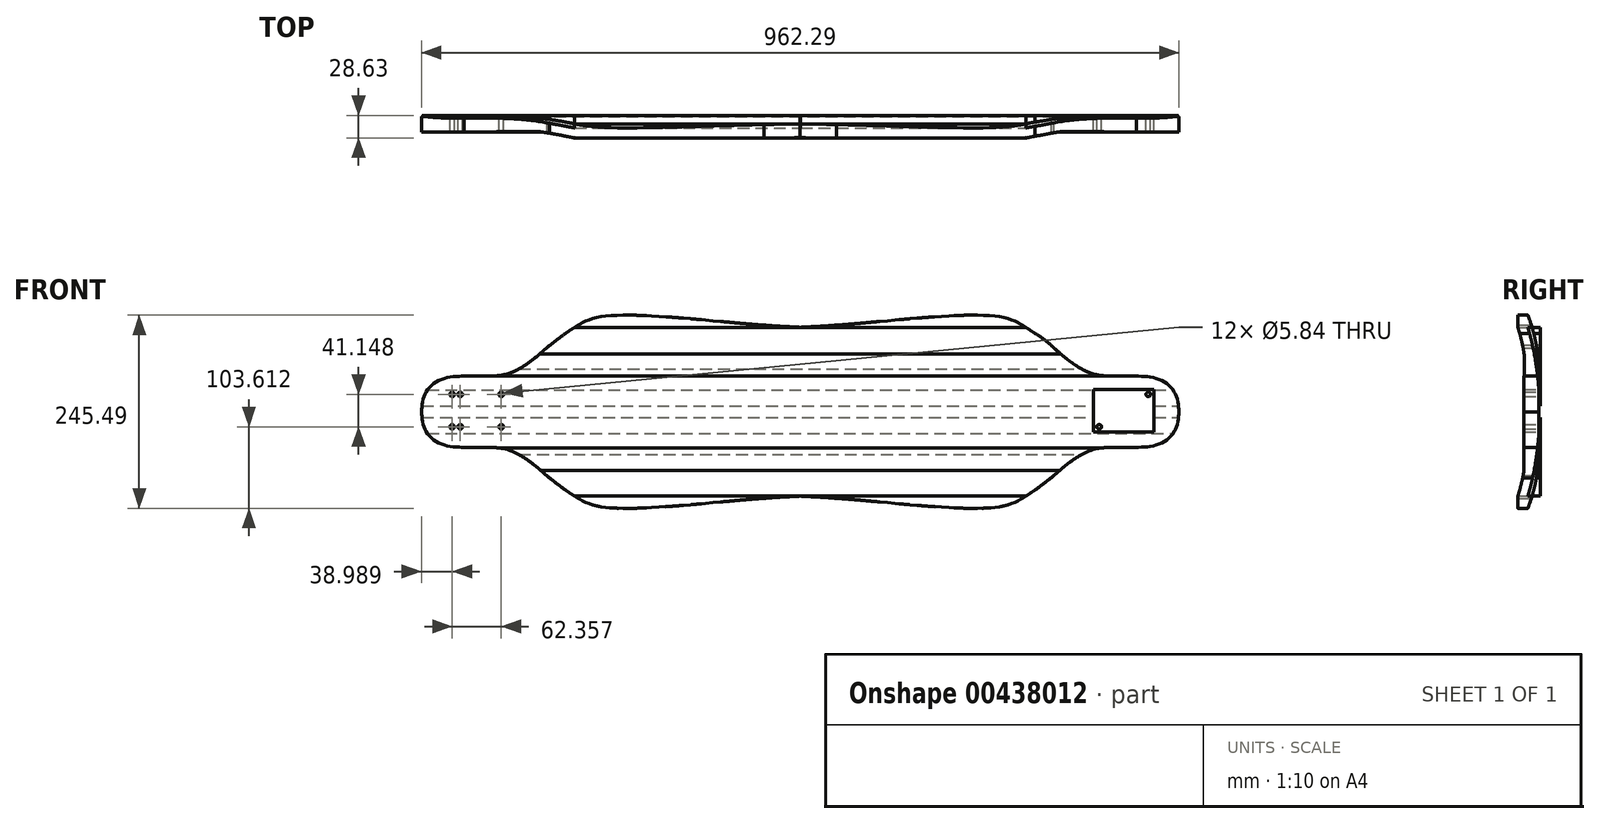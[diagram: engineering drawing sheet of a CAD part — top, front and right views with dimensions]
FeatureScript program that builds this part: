
annotation { "Feature Type Name" : "Feature", "Feature Type Description" : "" }
export const myFeature = defineFeature(function(context is Context, id is Id, definition is map)
    precondition{}
    {
        {
            var Q0;
            Q0=qCreatedBy(makeId("Front.planeOp"),FACE);
            var sketch = newSketch(context, id + "F0", { "sketchPlane" : qUnion([Q0])});
            skFitSpline(sketch, "E0.MirrorCS", {"points": [v(153.91, 111.97) * mm, v(126.22, 132.16) * mm, v(94.19, 138.32) * mm], "startDerivative": vector(-48.82, 48.29) * mm, "endDerivative": vector(-67.2, 5.62) * mm});
            skFitSpline(sketch, "E1.MirrorCS", {"points": [v(314.26, 80.32) * mm, v(259.22, 80.83) * mm, v(203.15, 79.33) * mm, v(126.22, 138.32) * mm], "startDerivative": vector(-184.89, 36.73) * mm, "endDerivative": vector(-208.9, 198.7) * mm});
            skFitSpline(sketch, "E2.MirrorCS", {"points": [v(153.91, -49.83) * mm, v(126.22, -70.02) * mm, v(94.19, -76.17) * mm], "startDerivative": vector(-48.82, -48.29) * mm, "endDerivative": vector(-67.2, -5.62) * mm});
            skFitSpline(sketch, "E3.MirrorCS", {"points": [v(314.26, -18.18) * mm, v(259.22, -18.69) * mm, v(203.15, -17.18) * mm, v(126.22, -76.17) * mm], "startDerivative": vector(-184.89, -36.73) * mm, "endDerivative": vector(-208.9, -198.7) * mm});
            skLineSegment(sketch, "E4", {"start": v(258.47, -14.52) * mm, "end": v(223.39, -14.47) * mm});
            skPoint(sketch, "E5.orphan", {"position": v(291.38, -20.7) * mm});
            skPoint(sketch, "E6.MirrorCS.0.internal.orphan", {"position": v(291.4, -22.2) * mm});
            skLineSegment(sketch, "E7.MirrorCS", {"start": v(258.47, 76.67) * mm, "end": v(223.39, 76.62) * mm});
            skPoint(sketch, "E8.orphan", {"position": v(288.53, 82.9) * mm});
            skPoint(sketch, "E9", {"position": v(-168.34, 36.66) * mm});
            skCircle(sketch, "E10.MirrorC", {"center": v(211.46, 11.94) * mm, "radius": 2.92 * mm});
            skCircle(sketch, "E11.MirrorC", {"center": v(273.82, 11.94) * mm, "radius": 2.92 * mm});
            skCircle(sketch, "E12.MirrorC", {"center": v(263.53, 11.94) * mm, "radius": 2.92 * mm});
            skCircle(sketch, "E13.MirrorC", {"center": v(273.82, 53.1) * mm, "radius": 2.92 * mm});
            skCircle(sketch, "E14.MirrorC", {"center": v(211.46, 53.1) * mm, "radius": 2.92 * mm});
            skCircle(sketch, "E15.MirrorC", {"center": v(263.53, 53.1) * mm, "radius": 2.92 * mm});
            skLineSegment(sketch, "E16.MirrorCS", {"start": v(281.05, 59.44) * mm, "end": v(204.1, 59.44) * mm});
            skLineSegment(sketch, "E17.MirrorCS", {"start": v(204.1, 59.44) * mm, "end": v(204.1, 5.6) * mm});
            skLineSegment(sketch, "E18.MirrorCS", {"start": v(281.05, 59.44) * mm, "end": v(281.05, 5.6) * mm});
            skLineSegment(sketch, "E19.MirrorCS", {"start": v(281.05, 5.6) * mm, "end": v(204.1, 5.6) * mm});
            skPoint(sketch, "E20.orphan", {"position": v(424.44, 75.27) * mm});
            skPoint(sketch, "E21.MirrorP", {"position": v(424.44, -13.13) * mm});
            skFitSpline(sketch, "E22.MirrorCS", {"points": [v(258.47, -14.52) * mm, v(279.76, -12.42) * mm, v(300.17, -2.22) * mm, v(310.38, 14.11) * mm, v(312.8, 31.07) * mm], "startDerivative": vector(67.24, 11.02) * mm, "endDerivative": vector(5.32, 67.13) * mm});
            skFitSpline(sketch, "E23.MirrorCS", {"points": [v(258.47, 76.67) * mm, v(279.76, 74.57) * mm, v(300.17, 64.36) * mm, v(310.38, 48.03) * mm, v(312.8, 31.07) * mm], "startDerivative": vector(67.24, -11.02) * mm, "endDerivative": vector(5.32, -67.13) * mm});
            skPoint(sketch, "E24.orphan", {"position": v(-761.13, 75.27) * mm});
            skPoint(sketch, "E25.orphan", {"position": v(315.71, 67.16) * mm});
            skPoint(sketch, "E26.end.orphan", {"position": v(315.71, -5.02) * mm});
            skPoint(sketch, "E27.orphan", {"position": v(-761.13, -13.13) * mm});
            skFitSpline(sketch, "E28.MirrorCS", {"points": [v(153.91, 111.97) * mm, v(118.25, 138.32) * mm, v(79.33, 152.54) * mm, v(-67.07, 145.75) * mm, v(-168.34, 138.32) * mm], "startDerivative": vector(-186.81, 155.51) * mm, "endDerivative": vector(-321.74, -14.8) * mm});
            skFitSpline(sketch, "E29.MirrorCS", {"points": [v(153.91, 111.97) * mm, v(118.25, 138.32) * mm, v(79.33, 152.54) * mm, v(-67.07, 145.75) * mm, v(-168.34, 138.32) * mm], "startDerivative": vector(-186.81, 155.51) * mm, "endDerivative": vector(-321.74, -14.8) * mm});
            skFitSpline(sketch, "E30.MirrorCS", {"points": [v(153.91, -49.83) * mm, v(118.25, -76.17) * mm, v(79.33, -90.4) * mm, v(-67.07, -83.6) * mm, v(-168.34, -76.17) * mm], "startDerivative": vector(-186.81, -155.51) * mm, "endDerivative": vector(-321.74, 14.8) * mm});
            skPoint(sketch, "E31.MirrorCS.end.orphan", {"position": v(-168.34, 127.37) * mm});
            skPoint(sketch, "E32.MirrorCS.end.orphan", {"position": v(-168.34, -65.22) * mm});
            skCircle(sketch, "E33.MirrorC", {"center": v(-610.5, 53.1) * mm, "radius": 2.92 * mm});
            skCircle(sketch, "E34.MirrorC", {"center": v(-600.21, 11.94) * mm, "radius": 2.92 * mm});
            skFitSpline(sketch, "E35.MirrorCS", {"points": [v(-490.6, -49.83) * mm, v(-462.9, -70.02) * mm, v(-430.87, -76.17) * mm], "startDerivative": vector(48.82, -48.29) * mm, "endDerivative": vector(67.2, -5.62) * mm});
            skFitSpline(sketch, "E36.MirrorCS", {"points": [v(-490.6, 111.97) * mm, v(-462.9, 132.16) * mm, v(-430.87, 138.32) * mm], "startDerivative": vector(48.82, 48.29) * mm, "endDerivative": vector(67.2, 5.62) * mm});
            skPoint(sketch, "E37.MirrorP", {"position": v(-652.4, 67.16) * mm});
            skPoint(sketch, "E38.MirrorP", {"position": v(-625.22, 82.9) * mm});
            skFitSpline(sketch, "E39.MirrorCS", {"points": [v(-490.6, 111.97) * mm, v(-454.93, 138.32) * mm, v(-416.02, 152.54) * mm, v(-269.61, 145.75) * mm, v(-168.34, 138.32) * mm], "startDerivative": vector(186.81, 155.51) * mm, "endDerivative": vector(321.74, -14.8) * mm});
            skCircle(sketch, "E40.MirrorC", {"center": v(-600.21, 53.1) * mm, "radius": 2.92 * mm});
            skCircle(sketch, "E41.MirrorC", {"center": v(-548.14, 53.1) * mm, "radius": 2.92 * mm});
            skCircle(sketch, "E42.MirrorC", {"center": v(-548.14, 11.94) * mm, "radius": 2.92 * mm});
            skCircle(sketch, "E43.MirrorC", {"center": v(-610.5, 11.94) * mm, "radius": 2.92 * mm});
            skPoint(sketch, "E44.MirrorP", {"position": v(-628.07, -20.7) * mm});
            skPoint(sketch, "E45.MirrorP", {"position": v(-652.4, -5.02) * mm});
            skFitSpline(sketch, "E46.MirrorCS", {"points": [v(-595.16, -14.52) * mm, v(-616.44, -12.42) * mm, v(-636.86, -2.22) * mm, v(-647.06, 14.11) * mm, v(-649.49, 31.07) * mm], "startDerivative": vector(-67.24, 11.02) * mm, "endDerivative": vector(-5.32, 67.13) * mm});
            skPoint(sketch, "E47.MirrorP", {"position": v(-628.09, -22.2) * mm});
            skFitSpline(sketch, "E48.MirrorCS", {"points": [v(-490.6, -49.83) * mm, v(-454.93, -76.17) * mm, v(-416.02, -90.4) * mm, v(-269.61, -83.6) * mm, v(-168.34, -76.17) * mm], "startDerivative": vector(186.81, -155.51) * mm, "endDerivative": vector(321.74, 14.8) * mm});
            skLineSegment(sketch, "E49.MirrorCS", {"start": v(-540.78, 59.44) * mm, "end": v(-540.78, 5.6) * mm});
            skFitSpline(sketch, "E50.MirrorCS", {"points": [v(-490.6, 111.97) * mm, v(-454.93, 138.32) * mm, v(-416.02, 152.54) * mm, v(-269.61, 145.75) * mm, v(-168.34, 138.32) * mm], "startDerivative": vector(186.81, 155.51) * mm, "endDerivative": vector(321.74, -14.8) * mm});
            skLineSegment(sketch, "E51.MirrorCS", {"start": v(-595.16, 76.67) * mm, "end": v(-560.08, 76.62) * mm});
            skLineSegment(sketch, "E52.MirrorCS", {"start": v(-595.16, -14.52) * mm, "end": v(-560.08, -14.47) * mm});
            skFitSpline(sketch, "E53.MirrorCS", {"points": [v(-650.94, -18.18) * mm, v(-595.9, -18.69) * mm, v(-539.83, -17.18) * mm, v(-462.9, -76.17) * mm], "startDerivative": vector(184.89, -36.73) * mm, "endDerivative": vector(208.9, -198.7) * mm});
            skLineSegment(sketch, "E54.MirrorCS", {"start": v(-617.74, 59.44) * mm, "end": v(-540.78, 59.44) * mm});
            skFitSpline(sketch, "E55.MirrorCS", {"points": [v(-650.94, 80.32) * mm, v(-595.9, 80.83) * mm, v(-539.83, 79.33) * mm, v(-462.9, 138.32) * mm], "startDerivative": vector(184.89, 36.73) * mm, "endDerivative": vector(208.9, 198.7) * mm});
            skLineSegment(sketch, "E56.MirrorCS", {"start": v(-617.74, 59.44) * mm, "end": v(-617.74, 5.6) * mm});
            skLineSegment(sketch, "E57.MirrorCS", {"start": v(-617.74, 5.6) * mm, "end": v(-540.78, 5.6) * mm});
            skFitSpline(sketch, "E58.MirrorCS", {"points": [v(-595.16, 76.67) * mm, v(-616.44, 74.57) * mm, v(-636.86, 64.36) * mm, v(-647.06, 48.03) * mm, v(-649.49, 31.07) * mm], "startDerivative": vector(-67.24, -11.02) * mm, "endDerivative": vector(-5.32, -67.13) * mm});
            skFitSpline(sketch, "E59", {"points": [v(-269.61, 145.75) * mm, v(-214.57, 141.12) * mm, v(-168.34, 139.72) * mm], "startDerivative": vector(107.74, -9.4) * mm, "endDerivative": vector(94.6, -2.55) * mm});
            skFitSpline(sketch, "E60.MirrorCS", {"points": [v(-67.07, 145.75) * mm, v(-122.12, 141.12) * mm, v(-168.34, 139.72) * mm], "startDerivative": vector(-107.74, -9.4) * mm, "endDerivative": vector(-94.6, -2.55) * mm});
            skFitSpline(sketch, "E61.MirrorCS", {"points": [v(-67.07, -83.6) * mm, v(-122.12, -78.98) * mm, v(-168.34, -77.58) * mm], "startDerivative": vector(-107.74, 9.4) * mm, "endDerivative": vector(-94.6, 2.55) * mm});
            skFitSpline(sketch, "E62.MirrorCS", {"points": [v(-269.61, -83.6) * mm, v(-214.57, -78.98) * mm, v(-168.34, -77.58) * mm], "startDerivative": vector(107.74, 9.4) * mm, "endDerivative": vector(94.6, 2.55) * mm});
            skPoint(sketch, "E63.orphan", {"position": v(-452.56, 31.07) * mm});
            skPoint(sketch, "E64.orphan", {"position": v(115.87, 31.07) * mm});
            skLineSegment(sketch, "E65.trimOffspring", {"start": v(-168.34, -76.17) * mm, "end": v(-168.34, -77.64) * mm});
            skPoint(sketch, "E66.start.orphan", {"position": v(-168.34, 150.96) * mm});
            skSolve(sketch);
        }
        {
            var Q0;
            Q0=makeQuery(id+"F0.imprint","IMPRINT",FACE,{"disambiguationData":[TD([[makeQuery(id+"F0.imprint","IMPRINT",EDGE,{"derivedFrom":sQuery(id+"F0.wireOp",EDGE,"54694fe5-f969-434b-b929-3ccada8eebf9")}),-1.0]])]});
            var Q1;
            Q1=makeQuery(id+"F0.imprint","IMPRINT",FACE,{"disambiguationData":[TD([[makeQuery(id+"F0.imprint","IMPRINT",EDGE,{"derivedFrom":sQuery(id+"F0.wireOp",EDGE,"02af59b5-e7f6-4803-9d26-3b46dd477805.right")}),-1.0]])]});
            var Q2;
            {var subQ0=sQuery(id+"F0.wireOp",EDGE,"062809b9-a678-4541-9586-a59974c6fc33.bottom");Q2=makeQuery(id+"F0.imprint","IMPRINT",FACE,{"disambiguationData":[TD([[makeQuery(id+"F0.imprint","IMPRINT",EDGE,{"derivedFrom":subQ0}),-1.0]])]});}
            var Q3;
            Q3=makeQuery(id+"F0.imprint","IMPRINT",FACE,{"disambiguationData":[TD([[makeQuery(id+"F0.imprint","IMPRINT",EDGE,{"derivedFrom":sQuery(id+"F0.wireOp",EDGE,"92bb7d47-26f2-429a-bf82-6a459e636457")}),-1.0]])]});
            var Q4;
            Q4=makeQuery(id+"F0.imprint","IMPRINT",FACE,{"disambiguationData":[TD([[makeQuery(id+"F0.imprint","IMPRINT",EDGE,{"derivedFrom":sQuery(id+"F0.wireOp",EDGE,"E10.MirrorC")}),1.0]])]});
            var Q5;
            Q5=makeQuery(id+"F0.imprint","IMPRINT",FACE,{"disambiguationData":[TD([[makeQuery(id+"F0.imprint","IMPRINT",EDGE,{"derivedFrom":sQuery(id+"F0.wireOp",EDGE,"89cd0182-1944-4f00-9323-803960b5a9c0")}),-1.0]])]});
            var Q6;
            Q6=makeQuery(id+"F0.imprint","IMPRINT",FACE,{"disambiguationData":[TD([[makeQuery(id+"F0.imprint","IMPRINT",EDGE,{"derivedFrom":sQuery(id+"F0.wireOp",EDGE,"062809b9-a678-4541-9586-a59974c6fc33.left")}),1.0]])]});
            var Q7;
            {var subQ0=sQuery(id+"F0.wireOp",EDGE,"b9591a49-4a40-4ac3-9c40-6eddea82a4450.MirrorCS");Q7=makeQuery(id+"F0.imprint","IMPRINT",FACE,{"disambiguationData":[TD([[makeQuery(id+"F0.imprint","IMPRINT",EDGE,{"derivedFrom":subQ0}),-1.0]])]});}
            var Q8;
            {var subQ0=sQuery(id+"F0.wireOp",EDGE,"f067fed3-db68-4427-a3f0-daf9bd1214f3");Q8=makeQuery(id+"F0.imprint","IMPRINT",FACE,{"disambiguationData":[TD([[makeQuery(id+"F0.imprint","IMPRINT",EDGE,{"derivedFrom":subQ0}),1.0]])]});}
            var Q9;
            {var subQ0=sQuery(id+"F0.wireOp",EDGE,"E32.MirrorCS");Q9=makeQuery(id+"F0.imprint","IMPRINT",FACE,{"disambiguationData":[TD([[makeQuery(id+"F0.imprint","IMPRINT",EDGE,{"derivedFrom":subQ0}),-1.0]])]});}
            var Q10;
            {var subQ0=sQuery(id+"F0.wireOp",EDGE,"E31.MirrorCS");Q10=makeQuery(id+"F0.imprint","IMPRINT",FACE,{"disambiguationData":[TD([[makeQuery(id+"F0.imprint","IMPRINT",EDGE,{"derivedFrom":subQ0}),1.0]])]});}
            var Q11;
            {var subQ12=sQuery(id+"F0.wireOp",EDGE,"E1.MirrorCS");Q11=makeQuery(id+"F0.imprint","IMPRINT",FACE,{"disambiguationData":[TD([[makeQuery(id+"F0.imprint","IMPRINT",EDGE,{"derivedFrom":subQ12}),1.0]])]});}
            var Q12;
            Q12=makeQuery(id+"F0.imprint","IMPRINT",FACE,{"disambiguationData":[TD([[makeQuery(id+"F0.imprint","IMPRINT",EDGE,{"derivedFrom":sQuery(id+"F0.wireOp",EDGE,"E46.MirrorCS")}),-1.0]])]});
            var Q13;
            {var subQ0=sQuery(id+"F0.wireOp",EDGE,"E359.MirrorCS");Q13=makeQuery(id+"F0.imprint","IMPRINT",FACE,{"disambiguationData":[TD([[makeQuery(id+"F0.imprint","IMPRINT",EDGE,{"derivedFrom":subQ0}),1.0]])]});}
            var Q14;
            {var subQ0=sQuery(id+"F0.wireOp",EDGE,"E358.MirrorCS");Q14=makeQuery(id+"F0.imprint","IMPRINT",FACE,{"disambiguationData":[TD([[makeQuery(id+"F0.imprint","IMPRINT",EDGE,{"derivedFrom":subQ0}),-1.0]])]});}
            var Q15;
            Q15=makeQuery(id+"F0.imprint","IMPRINT",FACE,{"disambiguationData":[TD([[makeQuery(id+"F0.imprint","IMPRINT",EDGE,{"derivedFrom":sQuery(id+"F0.wireOp",EDGE,"E13.MirrorC")}),1.0]])]});
            var Q16;
            Q16=makeQuery(id+"F0.imprint","IMPRINT",FACE,{"disambiguationData":[TD([[makeQuery(id+"F0.imprint","IMPRINT",EDGE,{"derivedFrom":sQuery(id+"F0.wireOp",EDGE,"E34.MirrorC")}),-1.0]])]});
            var Q17;
            Q17=makeQuery(id+"F0.imprint","IMPRINT",FACE,{"disambiguationData":[TD([[makeQuery(id+"F0.imprint","IMPRINT",EDGE,{"derivedFrom":sQuery(id+"F0.wireOp",EDGE,"E33.MirrorC")}),-1.0]])]});
            extrude(context, id + "F1", {"entities" : qUnion([Q0, Q1, Q2, Q3, Q4, Q5, Q6, Q7, Q8, Q9, Q10, Q11, Q12, Q13, Q14, Q15, Q16, Q17]), "depth" : 50.8 * mm});
        }
        {
            var Q0;
            Q0=makeQuery(id+"F1.opExtrude","CAP_FACE",FACE,{"disambiguationData":[OSD([sQuery(id+"F0.wireOp",EDGE,"02af59b5-e7f6-4803-9d26-3b46dd477805.left"),sQuery(id+"F0.wireOp",EDGE,"02af59b5-e7f6-4803-9d26-3b46dd477805.right"),sQuery(id+"F0.wireOp",EDGE,"54694fe5-f969-434b-b929-3ccada8eebf9"),sQuery(id+"F0.wireOp",EDGE,"9572b309-95b0-4d00-b009-9f7e73c3226a"),sQuery(id+"F0.wireOp",EDGE,"9ed70d03-f706-47da-8b4f-a9a363b289d10.MirrorCS"),sQuery(id+"F0.wireOp",EDGE,"E0.MirrorCS"),sQuery(id+"F0.wireOp",EDGE,"E1.MirrorCS"),sQuery(id+"F0.wireOp",EDGE,"E2.MirrorCS"),sQuery(id+"F0.wireOp",EDGE,"E3.MirrorCS"),sQuery(id+"F0.wireOp",EDGE,"E4"),sQuery(id+"F0.wireOp",EDGE,"E26"),sQuery(id+"F0.wireOp",EDGE,"E7.MirrorCS"),sQuery(id+"F0.wireOp",EDGE,"cba3995b-21b8-48ba-a17e-b84a468ee1200.MirrorCS"),sQuery(id+"F0.wireOp",EDGE,"9455ca8d-976e-4d45-868c-3e5ceae797750.MirrorCS"),sQuery(id+"F0.wireOp",EDGE,"bb437472-1cce-4c1d-80da-beb2af860ac20.MirrorCS"),sQuery(id+"F0.wireOp",EDGE,"1ed70d3d-ef56-45d5-8113-0e0346001ab10.MirrorCS"),sQuery(id+"F0.wireOp",EDGE,"96e13706-5ee7-4921-8a0b-7c01300654cf0.MirrorCS"),sQuery(id+"F0.wireOp",EDGE,"5faff583-b4fc-4a09-a63c-e9ec7a417d71.trimOffspring"),sQuery(id+"F0.wireOp",EDGE,"f067fed3-db68-4427-a3f0-daf9bd1214f3"),sQuery(id+"F0.wireOp",EDGE,"b9591a49-4a40-4ac3-9c40-6eddea82a4450.MirrorCS"),sQuery(id+"F0.wireOp",EDGE,"E32.MirrorCS"),sQuery(id+"F0.wireOp",EDGE,"E31.MirrorCS")])],"isStart":false});
            var sketch = newSketch(context, id + "F2", { "sketchPlane" : qUnion([Q0])});
            skLineSegment(sketch, "E67.bottom", {"start": v(-617.74, 56.54) * mm, "end": v(-540.78, 56.54) * mm});
            skLineSegment(sketch, "E67.top", {"start": v(-617.74, 2.69) * mm, "end": v(-540.78, 2.69) * mm});
            skLineSegment(sketch, "E67.left", {"start": v(-617.74, 56.54) * mm, "end": v(-617.74, 2.69) * mm});
            skLineSegment(sketch, "E67.right", {"start": v(-540.78, 56.54) * mm, "end": v(-540.78, 2.69) * mm});
            skCircle(sketch, "E68", {"center": v(-610.37, 50.19) * mm, "radius": 2.92 * mm});
            skCircle(sketch, "E69", {"center": v(-610.37, 9.04) * mm, "radius": 2.92 * mm});
            skCircle(sketch, "E70", {"center": v(-600.21, 50.19) * mm, "radius": 2.92 * mm});
            skCircle(sketch, "E71", {"center": v(-600.21, 9.04) * mm, "radius": 2.92 * mm});
            skCircle(sketch, "E72", {"center": v(-548.14, 9.04) * mm, "radius": 2.92 * mm});
            skCircle(sketch, "E73", {"center": v(-548.14, 50.19) * mm, "radius": 2.92 * mm});
            skLineSegment(sketch, "E74", {"start": v(-166.89, 125.92) * mm, "end": v(-166.89, -66.71) * mm});
            skLineSegment(sketch, "E75.MirrorCS", {"start": v(283.96, 56.54) * mm, "end": v(207, 56.54) * mm});
            skLineSegment(sketch, "E76.MirrorCS", {"start": v(207, 56.54) * mm, "end": v(207, 2.69) * mm});
            skLineSegment(sketch, "E77.MirrorCS", {"start": v(283.96, 2.69) * mm, "end": v(207, 2.69) * mm});
            skLineSegment(sketch, "E78.MirrorCS", {"start": v(283.96, 56.54) * mm, "end": v(283.96, 2.69) * mm});
            skCircle(sketch, "E79.MirrorC", {"center": v(276.6, 50.19) * mm, "radius": 2.92 * mm});
            skCircle(sketch, "E80.MirrorC", {"center": v(276.6, 9.04) * mm, "radius": 2.92 * mm});
            skCircle(sketch, "E81.MirrorC", {"center": v(266.43, 50.19) * mm, "radius": 2.92 * mm});
            skCircle(sketch, "E82.MirrorC", {"center": v(266.43, 9.04) * mm, "radius": 2.92 * mm});
            skCircle(sketch, "E83.MirrorC", {"center": v(214.36, 9.04) * mm, "radius": 2.92 * mm});
            skCircle(sketch, "E84.MirrorC", {"center": v(214.36, 50.19) * mm, "radius": 2.92 * mm});
            skSolve(sketch);
        }
        {
            var Q0;
            Q0=makeQuery(id+"F2.imprint","IMPRINT",FACE,{"disambiguationData":[TD([[makeQuery(id+"F2.imprint","IMPRINT",EDGE,{"derivedFrom":sQuery(id+"F2.wireOp",EDGE,"E68")}),1.0]])]});
            var Q1;
            Q1=makeQuery(id+"F2.imprint","IMPRINT",FACE,{"disambiguationData":[TD([[makeQuery(id+"F2.imprint","IMPRINT",EDGE,{"derivedFrom":sQuery(id+"F2.wireOp",EDGE,"E70")}),1.0]])]});
            var Q2;
            Q2=makeQuery(id+"F2.imprint","IMPRINT",FACE,{"disambiguationData":[TD([[makeQuery(id+"F2.imprint","IMPRINT",EDGE,{"derivedFrom":sQuery(id+"F2.wireOp",EDGE,"E71")}),1.0]])]});
            var Q3;
            Q3=makeQuery(id+"F2.imprint","IMPRINT",FACE,{"disambiguationData":[TD([[makeQuery(id+"F2.imprint","IMPRINT",EDGE,{"derivedFrom":sQuery(id+"F2.wireOp",EDGE,"E69")}),1.0]])]});
            var Q4;
            Q4=makeQuery(id+"F2.imprint","IMPRINT",FACE,{"disambiguationData":[TD([[makeQuery(id+"F2.imprint","IMPRINT",EDGE,{"derivedFrom":sQuery(id+"F2.wireOp",EDGE,"E72")}),1.0]])]});
            var Q5;
            Q5=makeQuery(id+"F2.imprint","IMPRINT",FACE,{"disambiguationData":[TD([[makeQuery(id+"F2.imprint","IMPRINT",EDGE,{"derivedFrom":sQuery(id+"F2.wireOp",EDGE,"E73")}),1.0]])]});
            var Q6;
            Q6=makeQuery(id+"F2.imprint","IMPRINT",FACE,{"disambiguationData":[TD([[makeQuery(id+"F2.imprint","IMPRINT",EDGE,{"derivedFrom":sQuery(id+"F2.wireOp",EDGE,"E84.MirrorC")}),-1.0]])]});
            var Q7;
            Q7=makeQuery(id+"F2.imprint","IMPRINT",FACE,{"disambiguationData":[TD([[makeQuery(id+"F2.imprint","IMPRINT",EDGE,{"derivedFrom":sQuery(id+"F2.wireOp",EDGE,"E83.MirrorC")}),-1.0]])]});
            var Q8;
            Q8=makeQuery(id+"F2.imprint","IMPRINT",FACE,{"disambiguationData":[TD([[makeQuery(id+"F2.imprint","IMPRINT",EDGE,{"derivedFrom":sQuery(id+"F2.wireOp",EDGE,"E82.MirrorC")}),-1.0]])]});
            var Q9;
            Q9=makeQuery(id+"F2.imprint","IMPRINT",FACE,{"disambiguationData":[TD([[makeQuery(id+"F2.imprint","IMPRINT",EDGE,{"derivedFrom":sQuery(id+"F2.wireOp",EDGE,"E80.MirrorC")}),-1.0]])]});
            var Q10;
            Q10=makeQuery(id+"F2.imprint","IMPRINT",FACE,{"disambiguationData":[TD([[makeQuery(id+"F2.imprint","IMPRINT",EDGE,{"derivedFrom":sQuery(id+"F2.wireOp",EDGE,"E79.MirrorC")}),-1.0]])]});
            var Q11;
            Q11=makeQuery(id+"F2.imprint","IMPRINT",FACE,{"disambiguationData":[TD([[makeQuery(id+"F2.imprint","IMPRINT",EDGE,{"derivedFrom":sQuery(id+"F2.wireOp",EDGE,"E81.MirrorC")}),-1.0]])]});
            extrude(context, id + "F3", {"entities" : qUnion([Q0, Q1, Q2, Q3, Q4, Q5, Q6, Q7, Q8, Q9, Q10, Q11]), "operationType" : NewBodyOperationType.REMOVE, "oppositeDirection" : true, "depth" : 25.4 * mm});
        }
        {
            var Q0;
            Q0=makeQuery(id+"F1.opExtrude","CAP_FACE",FACE,{"disambiguationData":[OSD([sQuery(id+"F0.wireOp",EDGE,"54694fe5-f969-434b-b929-3ccada8eebf9"),sQuery(id+"F0.wireOp",EDGE,"9572b309-95b0-4d00-b009-9f7e73c3226a"),sQuery(id+"F0.wireOp",EDGE,"9ed70d03-f706-47da-8b4f-a9a363b289d10.MirrorCS"),sQuery(id+"F0.wireOp",EDGE,"E0.MirrorCS"),sQuery(id+"F0.wireOp",EDGE,"E1.MirrorCS"),sQuery(id+"F0.wireOp",EDGE,"E2.MirrorCS"),sQuery(id+"F0.wireOp",EDGE,"E3.MirrorCS"),sQuery(id+"F0.wireOp",EDGE,"E4"),sQuery(id+"F0.wireOp",EDGE,"E7.MirrorCS"),sQuery(id+"F0.wireOp",EDGE,"9455ca8d-976e-4d45-868c-3e5ceae797750.MirrorCS"),sQuery(id+"F0.wireOp",EDGE,"5faff583-b4fc-4a09-a63c-e9ec7a417d71.trimOffspring"),sQuery(id+"F0.wireOp",EDGE,"f067fed3-db68-4427-a3f0-daf9bd1214f3"),sQuery(id+"F0.wireOp",EDGE,"b9591a49-4a40-4ac3-9c40-6eddea82a4450.MirrorCS"),sQuery(id+"F0.wireOp",EDGE,"E32.MirrorCS"),sQuery(id+"F0.wireOp",EDGE,"E31.MirrorCS"),sQuery(id+"F0.wireOp",EDGE,"92bb7d47-26f2-429a-bf82-6a459e636457"),sQuery(id+"F0.wireOp",EDGE,"b6ba227c-8afe-4edb-aedd-f0549fda6e15"),sQuery(id+"F0.wireOp",EDGE,"793bed87-008b-41f4-bf6e-c205d1063800"),sQuery(id+"F0.wireOp",EDGE,"28036a85-de49-4989-b8b5-f112d6133179"),sQuery(id+"F0.wireOp",EDGE,"89cd0182-1944-4f00-9323-803960b5a9c0"),sQuery(id+"F0.wireOp",EDGE,"6373697f-7fe0-442c-b118-95b429602822"),sQuery(id+"F0.wireOp",EDGE,"E10.MirrorC"),sQuery(id+"F0.wireOp",EDGE,"E11.MirrorC"),sQuery(id+"F0.wireOp",EDGE,"E12.MirrorC"),sQuery(id+"F0.wireOp",EDGE,"E13.MirrorC"),sQuery(id+"F0.wireOp",EDGE,"E14.MirrorC"),sQuery(id+"F0.wireOp",EDGE,"E15.MirrorC"),sQuery(id+"F0.wireOp",EDGE,"cea14af6-60e8-406b-8ace-559b2c7d7bdf"),sQuery(id+"F0.wireOp",EDGE,"2c7a5f25-ea35-4496-83f1-23e8682bbf5f1.MirrorCS"),sQuery(id+"F0.wireOp",EDGE,"2c7a5f25-ea35-4496-83f1-23e8682bbf5f5.MirrorC"),sQuery(id+"F0.wireOp",EDGE,"2c7a5f25-ea35-4496-83f1-23e8682bbf5f8.MirrorCS"),sQuery(id+"F0.wireOp",EDGE,"E22.MirrorCS"),sQuery(id+"F0.wireOp",EDGE,"E23.MirrorCS")])],"isStart":false});
            extrude(context, id + "F4", {"entities" : qUnion([Q0]), "depth" : 1.27 * mm});
        }
        {
            var Q0;
            Q0=makeQuery(id+"F4.opExtrude","SWEPT_BODY",BODY,{"disambiguationData":[OSD([sQuery(id+"F0.wireOp",EDGE,"54694fe5-f969-434b-b929-3ccada8eebf9"),sQuery(id+"F0.wireOp",EDGE,"9572b309-95b0-4d00-b009-9f7e73c3226a"),sQuery(id+"F0.wireOp",EDGE,"9ed70d03-f706-47da-8b4f-a9a363b289d10.MirrorCS"),sQuery(id+"F0.wireOp",EDGE,"E0.MirrorCS"),sQuery(id+"F0.wireOp",EDGE,"E1.MirrorCS"),sQuery(id+"F0.wireOp",EDGE,"E2.MirrorCS"),sQuery(id+"F0.wireOp",EDGE,"E3.MirrorCS"),sQuery(id+"F0.wireOp",EDGE,"E4"),sQuery(id+"F0.wireOp",EDGE,"E7.MirrorCS"),sQuery(id+"F0.wireOp",EDGE,"9455ca8d-976e-4d45-868c-3e5ceae797750.MirrorCS"),sQuery(id+"F0.wireOp",EDGE,"5faff583-b4fc-4a09-a63c-e9ec7a417d71.trimOffspring"),sQuery(id+"F0.wireOp",EDGE,"f067fed3-db68-4427-a3f0-daf9bd1214f3"),sQuery(id+"F0.wireOp",EDGE,"b9591a49-4a40-4ac3-9c40-6eddea82a4450.MirrorCS"),sQuery(id+"F0.wireOp",EDGE,"E32.MirrorCS"),sQuery(id+"F0.wireOp",EDGE,"E31.MirrorCS"),sQuery(id+"F0.wireOp",EDGE,"92bb7d47-26f2-429a-bf82-6a459e636457"),sQuery(id+"F0.wireOp",EDGE,"b6ba227c-8afe-4edb-aedd-f0549fda6e15"),sQuery(id+"F0.wireOp",EDGE,"793bed87-008b-41f4-bf6e-c205d1063800"),sQuery(id+"F0.wireOp",EDGE,"28036a85-de49-4989-b8b5-f112d6133179"),sQuery(id+"F0.wireOp",EDGE,"89cd0182-1944-4f00-9323-803960b5a9c0"),sQuery(id+"F0.wireOp",EDGE,"6373697f-7fe0-442c-b118-95b429602822"),sQuery(id+"F0.wireOp",EDGE,"E10.MirrorC"),sQuery(id+"F0.wireOp",EDGE,"E11.MirrorC"),sQuery(id+"F0.wireOp",EDGE,"E12.MirrorC"),sQuery(id+"F0.wireOp",EDGE,"E13.MirrorC"),sQuery(id+"F0.wireOp",EDGE,"E14.MirrorC"),sQuery(id+"F0.wireOp",EDGE,"E15.MirrorC"),sQuery(id+"F0.wireOp",EDGE,"cea14af6-60e8-406b-8ace-559b2c7d7bdf"),sQuery(id+"F0.wireOp",EDGE,"2c7a5f25-ea35-4496-83f1-23e8682bbf5f1.MirrorCS"),sQuery(id+"F0.wireOp",EDGE,"2c7a5f25-ea35-4496-83f1-23e8682bbf5f5.MirrorC"),sQuery(id+"F0.wireOp",EDGE,"2c7a5f25-ea35-4496-83f1-23e8682bbf5f8.MirrorCS"),sQuery(id+"F0.wireOp",EDGE,"E22.MirrorCS"),sQuery(id+"F0.wireOp",EDGE,"E23.MirrorCS")])]});
            deleteBodies(context, id + "F5", {"entities" : qUnion([Q0])});
        }
        {
            var Q0;
            Q0=qCreatedBy(makeId("Right.planeOp"),FACE);
            cPlane(context, id + "F6", {"entities" : qUnion([Q0]), "cplaneType" : CPlaneType.OFFSET, "offset" : 330.2 * mm, "width" : 152.4 * mm, "height" : 152.4 * mm});
        }
        {
            var Q0;
            Q0=qCreatedBy(id+"F6.planeOp",FACE);
            var sketch = newSketch(context, id + "F7", { "sketchPlane" : qUnion([Q0])});
            skLineSegment(sketch, "E85.bottom", {"start": v(-48.15, -76.19) * mm, "end": v(0, -76.19) * mm});
            skLineSegment(sketch, "E85.right", {"start": v(0, -76.19) * mm, "end": v(0, 123.87) * mm});
            skFitSpline(sketch, "E86.MirrorCS", {"points": [v(-15.93, 138.33) * mm, v(-6.62, 98.44) * mm, v(0, 38.3) * mm], "startDerivative": vector(23.4, -79.2) * mm, "endDerivative": vector(9.06, -120.52) * mm});
            skLineSegment(sketch, "E87", {"start": v(-15.93, -76.19) * mm, "end": v(-28.63, -76.19) * mm});
            skFitSpline(sketch, "E88", {"points": [v(-28.63, -76.19) * mm, v(-20.04, -37.9) * mm, v(-17.25, 31.07) * mm], "startDerivative": vector(27.5, 88.82) * mm, "endDerivative": vector(-0.53, 124.55) * mm});
            skFitSpline(sketch, "E89.MirrorCS", {"points": [v(-28.63, 138.33) * mm, v(-20.04, 100.04) * mm, v(-17.25, 31.07) * mm], "startDerivative": vector(27.5, -88.82) * mm, "endDerivative": vector(-0.53, -124.55) * mm});
            skLineSegment(sketch, "E90", {"start": v(-28.63, 138.33) * mm, "end": v(-28.34, 138.33) * mm});
            skLineSegment(sketch, "E91", {"start": v(0, 23.84) * mm, "end": v(0, 38.3) * mm});
            skLineSegment(sketch, "E92", {"start": v(-17.15, 54.74) * mm, "end": v(-17.15, 7.4) * mm});
            skLineSegment(sketch, "E93", {"start": v(0, 123.87) * mm, "end": v(0, 138.52) * mm});
            skLineSegment(sketch, "E94", {"start": v(-15.93, 138.33) * mm, "end": v(0, 138.33) * mm});
            skLineSegment(sketch, "E95", {"start": v(0, 138.33) * mm, "end": v(-15.93, 138.33) * mm});
            skLineSegment(sketch, "E96", {"start": v(-52.48, 138.33) * mm, "end": v(-53.99, -76.19) * mm});
            skLineSegment(sketch, "E97", {"start": v(-53.99, -76.19) * mm, "end": v(-48.15, -76.19) * mm});
            skLineSegment(sketch, "E98", {"start": v(-22.28, 138.33) * mm, "end": v(-22.28, 155.69) * mm});
            skLineSegment(sketch, "E99", {"start": v(-28.63, 142.12) * mm, "end": v(-28.63, 154.1) * mm});
            skLineSegment(sketch, "E100", {"start": v(-28.63, 154.1) * mm, "end": v(-15.93, 154.1) * mm});
            skArc(sketch, "E101.filletArc", {"start": v(-28.63, 142.12) * mm, "mid": v(-28.36, 138.43) * mm, "end": v(-27.55, 134.81) * mm});
            skLineSegment(sketch, "E102.MirrorCS", {"start": v(-28.63, -76.19) * mm, "end": v(-28.34, -76.19) * mm});
            skArc(sketch, "E103.MirrorCS", {"start": v(-28.63, -79.98) * mm, "mid": v(-28.36, -76.29) * mm, "end": v(-27.55, -72.67) * mm});
            skLineSegment(sketch, "E104.MirrorCS", {"start": v(-15.93, -76.19) * mm, "end": v(0, -76.19) * mm});
            skFitSpline(sketch, "E105.MirrorCS", {"points": [v(-28.63, -76.19) * mm, v(-20.04, -37.9) * mm, v(-17.25, 31.07) * mm], "startDerivative": vector(27.5, 88.82) * mm, "endDerivative": vector(-0.53, 124.55) * mm});
            skLineSegment(sketch, "E106.MirrorCS", {"start": v(-28.63, -91.95) * mm, "end": v(-15.93, -91.95) * mm});
            skFitSpline(sketch, "E107.MirrorCS", {"points": [v(-15.93, -76.19) * mm, v(-6.62, -36.3) * mm, v(0, 23.84) * mm], "startDerivative": vector(23.4, 79.2) * mm, "endDerivative": vector(9.06, 120.52) * mm});
            skLineSegment(sketch, "E108.MirrorCS", {"start": v(0, -76.19) * mm, "end": v(-52.48, -76.19) * mm});
            skLineSegment(sketch, "E109.MirrorCS", {"start": v(0, -61.73) * mm, "end": v(0, -76.37) * mm});
            skLineSegment(sketch, "E110.MirrorCS", {"start": v(-28.63, -79.98) * mm, "end": v(-28.63, -91.95) * mm});
            skLineSegment(sketch, "E111.MirrorCS", {"start": v(-22.28, -76.19) * mm, "end": v(-22.28, -93.54) * mm});
            skLineSegment(sketch, "E112", {"start": v(-52.48, 138.33) * mm, "end": v(-52.48, 162.03) * mm});
            skLineSegment(sketch, "E113", {"start": v(-52.48, 162.03) * mm, "end": v(24.08, 159.46) * mm});
            skLineSegment(sketch, "E114", {"start": v(24.08, 159.46) * mm, "end": v(-0.26, 137.33) * mm});
            skLineSegment(sketch, "E115", {"start": v(-53.99, -76.19) * mm, "end": v(-80.3, -110.8) * mm});
            skLineSegment(sketch, "E116", {"start": v(-80.3, -110.8) * mm, "end": v(20.37, -120.62) * mm});
            skLineSegment(sketch, "E117", {"start": v(20.37, -120.62) * mm, "end": v(0, -76.19) * mm});
            skLineSegment(sketch, "E118", {"start": v(-1.66, 3.73) * mm, "end": v(-1.66, 31.07) * mm});
            skPoint(sketch, "E118.endSnap0", {"position": v(0, 31.07) * mm});
            skLineSegment(sketch, "E119", {"start": v(-1.66, 31.07) * mm, "end": v(-1.91, 31.11) * mm});
            skLineSegment(sketch, "E120.MirrorCS", {"start": v(-1.66, 58.41) * mm, "end": v(-1.66, 31.07) * mm});
            skLineSegment(sketch, "E121", {"start": v(-18.61, 31.07) * mm, "end": v(-19.22, 31.07) * mm});
            skPoint(sketch, "E122.MirrorCS.end.orphan", {"position": v(-18.61, 31.07) * mm});
            skPoint(sketch, "E122.MirrorCS.start.orphan", {"position": v(-18.61, 84.71) * mm});
            skPoint(sketch, "E123.start.orphan", {"position": v(-18.61, -22.57) * mm});
            skLineSegment(sketch, "E124", {"start": v(-20.8, -43.48) * mm, "end": v(-20.6, 104.17) * mm});
            skLineSegment(sketch, "E125", {"start": v(-20.6, 104.17) * mm, "end": v(-21.65, 104) * mm});
            skPoint(sketch, "E126.MirrorCS.end.orphan", {"position": v(-19.5, 31.07) * mm});
            skPoint(sketch, "E126.MirrorCS.start.orphan", {"position": v(-19.5, 95.16) * mm});
            skPoint(sketch, "E127.start.orphan", {"position": v(-19.5, -33.02) * mm});
            skLineSegment(sketch, "E128", {"start": v(-1.66, 3.73) * mm, "end": v(-1.66, -23.27) * mm});
            skFitSpline(sketch, "E129", {"points": [v(-1.66, -23.27) * mm, v(-6.5, -60.55) * mm, v(-15.93, -91.95) * mm], "startDerivative": vector(-6.72, -73.93) * mm, "endDerivative": vector(-22, -63.32) * mm});
            skPoint(sketch, "E130.orphan", {"position": v(-15.93, -79.8) * mm});
            skPoint(sketch, "E131.orphan", {"position": v(-14.95, -72.83) * mm});
            skPoint(sketch, "E132.orphan", {"position": v(-15.93, 141.95) * mm});
            skPoint(sketch, "E133.filletArc.end.orphan", {"position": v(-14.95, 134.98) * mm});
            skLineSegment(sketch, "E134.trimOffspring", {"start": v(-22.28, 138.33) * mm, "end": v(-52.48, 138.33) * mm});
            skLineSegment(sketch, "E135.MirrorCS", {"start": v(0, 38.3) * mm, "end": v(0, 23.84) * mm});
            skLineSegment(sketch, "E136.MirrorCS", {"start": v(0, 138.33) * mm, "end": v(-52.48, 138.33) * mm});
            skLineSegment(sketch, "E137.MirrorCS", {"start": v(-48.15, 138.33) * mm, "end": v(0, 138.33) * mm});
            skLineSegment(sketch, "E138.MirrorCS", {"start": v(20.37, 182.76) * mm, "end": v(0, 138.33) * mm});
            skFitSpline(sketch, "E139.MirrorCS", {"points": [v(-15.93, 138.33) * mm, v(-6.62, 98.44) * mm, v(0, 38.3) * mm], "startDerivative": vector(23.4, -79.2) * mm, "endDerivative": vector(9.06, -120.52) * mm});
            skFitSpline(sketch, "E140.MirrorCS", {"points": [v(-1.66, 85.4) * mm, v(-6.5, 122.7) * mm, v(-15.93, 154.1) * mm], "startDerivative": vector(-6.72, 73.93) * mm, "endDerivative": vector(-22, 63.32) * mm});
            skLineSegment(sketch, "E141.MirrorCS", {"start": v(-1.66, 58.41) * mm, "end": v(-1.66, 85.4) * mm});
            skLineSegment(sketch, "E142.MirrorCS", {"start": v(0, 138.33) * mm, "end": v(0, -61.73) * mm});
            skSolve(sketch);
        }
        {
            var Q0;
            {var subQ3=sQuery(id+"F7.wireOp",EDGE,"E96");Q0=makeQuery(id+"F7.imprint","IMPRINT",FACE,{"disambiguationData":[TD([[makeQuery(id+"F7.imprint","IMPRINT",EDGE,{"derivedFrom":subQ3}),1.0]])]});}
            var Q1;
            {var subQ3=sQuery(id+"F7.wireOp",EDGE,"e4161faf-2b02-4ce5-9694-c5f839d38700");Q1=makeQuery(id+"F7.imprint","IMPRINT",FACE,{"disambiguationData":[TD([[makeQuery(id+"F7.imprint","IMPRINT",EDGE,{"derivedFrom":subQ3}),-1.0]])]});}
            var Q2;
            {var subQ1=sQuery(id+"F7.wireOp",EDGE,"E97");Q2=makeQuery(id+"F7.imprint","IMPRINT",FACE,{"disambiguationData":[TD([[makeQuery(id+"F7.imprint","IMPRINT",EDGE,{"derivedFrom":subQ1}),-1.0]])]});}
            var Q3;
            {var subQ0=sQuery(id+"F7.wireOp",EDGE,"E107.MirrorCS");Q3=makeQuery(id+"F7.imprint","IMPRINT",FACE,{"disambiguationData":[TD([[makeQuery(id+"F7.imprint","IMPRINT",EDGE,{"derivedFrom":subQ0}),-1.0]])]});}
            var Q4;
            {var subQ6=sQuery(id+"F7.wireOp",EDGE,"E86.MirrorCS");Q4=makeQuery(id+"F7.imprint","IMPRINT",FACE,{"disambiguationData":[TD([[makeQuery(id+"F7.imprint","IMPRINT",EDGE,{"derivedFrom":subQ6}),1.0]])]});}
            var Q5;
            {var subQ6=sQuery(id+"F7.wireOp",EDGE,"E99");Q5=makeQuery(id+"F7.imprint","IMPRINT",FACE,{"disambiguationData":[TD([[makeQuery(id+"F7.imprint","IMPRINT",EDGE,{"derivedFrom":subQ6}),1.0]])]});}
            var Q6;
            {var subQ0=sQuery(id+"F7.wireOp",EDGE,"E91");Q6=makeQuery(id+"F7.imprint","IMPRINT",FACE,{"disambiguationData":[TD([[makeQuery(id+"F7.imprint","IMPRINT",EDGE,{"derivedFrom":subQ0}),1.0]])]});}
            var Q7;
            {var subQ4=sQuery(id+"F7.wireOp",EDGE,"E123");Q7=makeQuery(id+"F7.imprint","IMPRINT",FACE,{"disambiguationData":[TD([[makeQuery(id+"F7.imprint","IMPRINT",EDGE,{"derivedFrom":subQ4}),-1.0]])]});}
            var Q8;
            {var subQ1=sQuery(id+"F7.wireOp",EDGE,"E139.MirrorCS");Q8=makeQuery(id+"F7.imprint","IMPRINT",FACE,{"disambiguationData":[TD([[makeQuery(id+"F7.imprint","IMPRINT",EDGE,{"derivedFrom":subQ1}),1.0]])]});}
            var Q9;
            {var subQ0=sQuery(id+"F7.wireOp",EDGE,"E107.MirrorCS");Q9=makeQuery(id+"F7.imprint","IMPRINT",FACE,{"disambiguationData":[TD([[makeQuery(id+"F7.imprint","IMPRINT",EDGE,{"derivedFrom":subQ0}),1.0]])]});}
            extrude(context, id + "F8", {"entities" : qUnion([Q0, Q1, Q2, Q3, Q4, Q5, Q6, Q7, Q8, Q9]), "operationType" : NewBodyOperationType.REMOVE, "oppositeDirection" : true, "depth" : 1524 * mm});
        }
        {
            var Q0;
            Q0=qCreatedBy(makeId("Front.planeOp"),FACE);
            cPlane(context, id + "F9", {"entities" : qUnion([Q0]), "cplaneType" : CPlaneType.OFFSET, "offset" : 21.59 * mm, "width" : 152.4 * mm, "height" : 152.4 * mm});
        }
        {
            var Q0;
            Q0=qCreatedBy(id+"F9.planeOp",FACE);
            var sketch = newSketch(context, id + "F10", { "sketchPlane" : qUnion([Q0])});
            skLineSegment(sketch, "E143.bottom", {"start": v(-710.69, 76.8) * mm, "end": v(383.33, 76.8) * mm});
            skLineSegment(sketch, "E143.top", {"start": v(-710.69, -14.65) * mm, "end": v(383.33, -14.65) * mm});
            skLineSegment(sketch, "E143.left", {"start": v(-710.69, 76.8) * mm, "end": v(-710.69, -14.65) * mm});
            skLineSegment(sketch, "E143.right", {"start": v(383.33, 76.8) * mm, "end": v(383.33, -14.65) * mm});
            skSolve(sketch);
        }
        {
            var Q0;
            Q0=makeQuery(id+"F10.imprint","IMPRINT",FACE,{"disambiguationData":[TD([[makeQuery(id+"F10.imprint","IMPRINT",EDGE,{"derivedFrom":sQuery(id+"F10.wireOp",EDGE,"E143.bottom")}),-1.0]])]});
            extrude(context, id + "F11", {"entities" : qUnion([Q0]), "operationType" : NewBodyOperationType.REMOVE, "oppositeDirection" : true, "depth" : 13.5 * mm});
        }
        {
            var Q0;
            Q0=makeQuery(id+"F11.boolean.opBoolean","COPY",FACE,{"derivedFrom":makeQuery(id+"F11.opExtrude","CAP_FACE",FACE,{"disambiguationData":[OSD([sQuery(id+"F10.wireOp",EDGE,"E143.bottom"),sQuery(id+"F10.wireOp",EDGE,"E143.top"),sQuery(id+"F10.wireOp",EDGE,"E143.left"),sQuery(id+"F10.wireOp",EDGE,"E143.right")])],"isStart":false})});
            extrude(context, id + "F12", {"entities" : qUnion([Q0]), "operationType" : NewBodyOperationType.ADD, "depth" : 12.7 * mm});
        }
    });
